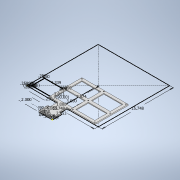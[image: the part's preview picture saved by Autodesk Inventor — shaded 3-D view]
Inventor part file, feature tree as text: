
AUTODESK INVENTOR PART (.ipt)
format: ipt  version: 2020 (Build 240168000, 168)  size: 296,960 bytes
history: native  units: in
note: dims shown in document units (in); Inventor stores cm internally (conversion verified against a paired STEP export)
features: extrude x4, sketch x3, hole x2, pattern_linear x1
ambient origin geometry x8: Origin, YZ Plane, XZ Plane, XY Plane, X Axis, Y Axis, Z Axis, Center Point
bodies: Solid1 (feature_tree)
feature tree (10):
  sketch  "Sketch1"  dims[d0=3.0in d1=2.0in]
  extrude  "Extrusion1"  Depth=2.0in
  hole  "Hole1"  [1 undecoded]
  sketch  "Sketch2"  dims[d2=0.25in d3=1.0in]
  extrude  "Extrusion2"  TaperAngle=0.0deg  [1 undecoded]
  hole  "Hole2"  [1 undecoded]
  extrude  "Extrusion3"  Depth=0.5in
  pattern_linear  "Rectangular Pattern1"  Spacing1=0.25in  [1 undecoded]
  extrude  "Extrusion4"  Depth=0.25in
  sketch  "Sketch3"  dims[d4=1.0in d5=0.0in d6=0.5in d7=0.5in d8=0.25in d9=0.25in d10=2.9528in d11=90.0deg d12=2.9528in d13=1.0in d14=7.874in d15=90.0deg d16=15.748in d17=15.748in d18=0.25in d19=0.0in d20=0.26in d21=0.5in d22=0.375in d23=0.25in d24=0.5635in d25=1.0in d26=0.8108in d27=0.25in d28=90.0deg d29=0.25in d30=0.25in d31=0.25in d32=4.3386in d33=2.9134in d34=0.25in d35=0.25in d36=0.25in d37=0.25in d38=0.25in d39=0.315in d40=90.0deg d41=0.0787in d42=0.0787in d43=0.0787in d44=0.0787in d45=0.0in d46=0.0in d47=0.203in d48=0.625in d49=0.375in d50=0.25in d51=0.5635in d52=1.0in d53=0.8108in d54=0.0787in d55=0.0in d56=1.1811in d58=4.839in d59=1.5748in d61=3.423in d62=0.25in d63=0.25in d64=0.0in d65=0.0in d66=0.25in]
note: 4 required parameter values undecoded (feature->parameter linkage not recoverable at this tier; creation-order binding heuristic only, values carry confidence <= 0.55)
